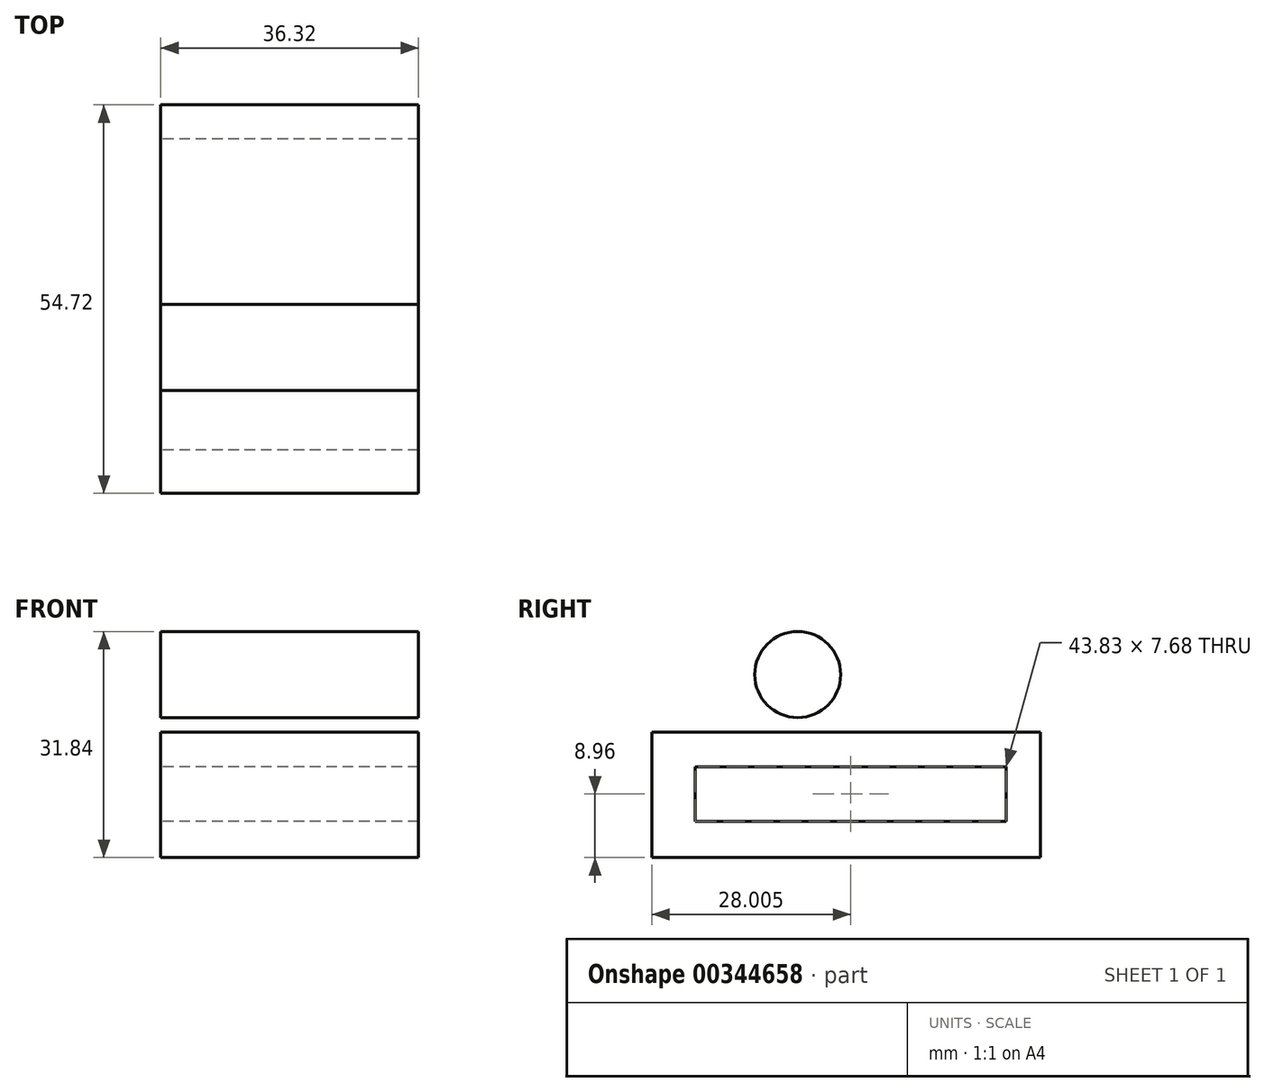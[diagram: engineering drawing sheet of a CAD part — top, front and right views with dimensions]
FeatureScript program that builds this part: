
annotation { "Feature Type Name" : "Feature", "Feature Type Description" : "" }
export const myFeature = defineFeature(function(context is Context, id is Id, definition is map)
    precondition{}
    {
        {
            var Q0;
            Q0=qCreatedBy(makeId("Right.planeOp"),FACE);
            var sketch = newSketch(context, id + "F0", { "sketchPlane" : qUnion([Q0])});
            skLineSegment(sketch, "E0.bottom", {"start": v(0, 0) * mm, "end": v(54.72, 0) * mm});
            skLineSegment(sketch, "E0.top", {"start": v(0, -17.7) * mm, "end": v(54.72, -17.7) * mm});
            skLineSegment(sketch, "E0.left", {"start": v(0, 0) * mm, "end": v(0, -17.7) * mm});
            skLineSegment(sketch, "E0.right", {"start": v(54.72, 0) * mm, "end": v(54.72, -17.7) * mm});
            skLineSegment(sketch, "E1.bottom", {"start": v(6.09, -4.89) * mm, "end": v(49.92, -4.89) * mm});
            skLineSegment(sketch, "E1.top", {"start": v(6.09, -12.57) * mm, "end": v(49.92, -12.57) * mm});
            skLineSegment(sketch, "E1.left", {"start": v(6.09, -4.89) * mm, "end": v(6.09, -12.57) * mm});
            skLineSegment(sketch, "E1.right", {"start": v(49.92, -4.89) * mm, "end": v(49.92, -12.57) * mm});
            skCircle(sketch, "E2", {"center": v(20.53, 8.1) * mm, "radius": 6.06 * mm});
            skSolve(sketch);
        }
        {
            var Q0;
            Q0 = qSketchRegion(id + "F0", true);
            extrude(context, id + "F1", {"entities" : qUnion([Q0]), "depth" : 36.32 * mm});
        }
        {
            var Q0;
            Q0 = qSketchRegion(id + "F0", true);
            extrude(context, id + "F2", {"entities" : qUnion([Q0]), "operationType" : NewBodyOperationType.ADD, "depth" : 25.4 * mm});
        }
    });
